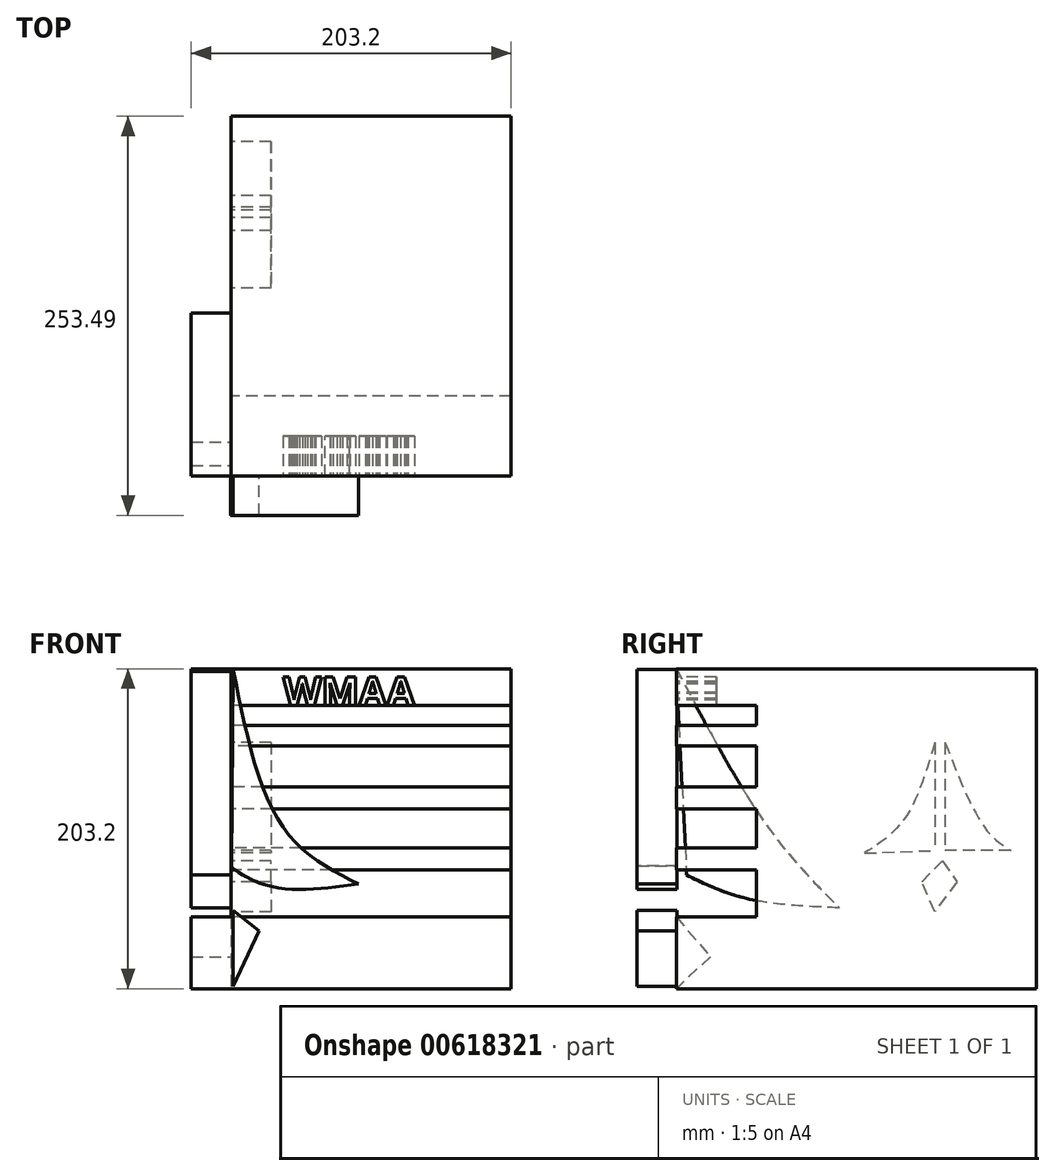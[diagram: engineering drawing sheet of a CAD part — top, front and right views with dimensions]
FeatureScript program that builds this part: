
annotation { "Feature Type Name" : "Feature", "Feature Type Description" : "" }
export const myFeature = defineFeature(function(context is Context, id is Id, definition is map)
    precondition{}
    {
        {
            var Q0;
            Q0=qCreatedBy(makeId("Front.planeOp"),FACE);
            var sketch = newSketch(context, id + "F0", { "sketchPlane" : qUnion([Q0])});
            skLineSegment(sketch, "E0.bottom", {"start": v(88.9, -101.6) * mm, "end": v(-88.9, -101.6) * mm});
            skLineSegment(sketch, "E0.top", {"start": v(88.9, 101.6) * mm, "end": v(-88.9, 101.6) * mm});
            skLineSegment(sketch, "E0.left", {"start": v(88.9, -101.6) * mm, "end": v(88.9, 101.6) * mm});
            skLineSegment(sketch, "E0.right", {"start": v(-88.9, -101.6) * mm, "end": v(-88.9, 101.6) * mm});
            skPoint(sketch, "E0.middle", {"position": v(0, 0) * mm});
            skSolve(sketch);
        }
        {
            var Q0;
            Q0=makeQuery(id+"F0.imprint","IMPRINT",FACE,{"disambiguationData":[TD([[makeQuery(id+"F0.imprint","IMPRINT",EDGE,{"derivedFrom":sQuery(id+"F0.wireOp",EDGE,"E0.bottom")}),-1.0]])]});
            extrude(context, id + "F1", {"entities" : qUnion([Q0]), "depth" : 177.8 * mm, "offsetDistance" : 25.4 * mm});
        }
        {
            var Q0;
            Q0=makeQuery(id+"F1.opExtrude","CAP_FACE",FACE,{"disambiguationData":[OSD([sQuery(id+"F0.wireOp",EDGE,"E0.bottom"),sQuery(id+"F0.wireOp",EDGE,"E0.top"),sQuery(id+"F0.wireOp",EDGE,"E0.left"),sQuery(id+"F0.wireOp",EDGE,"E0.right")])],"isStart":false});
            var sketch = newSketch(context, id + "F2", { "sketchPlane" : qUnion([Q0])});
            skLineSegment(sketch, "E1.bottom", {"start": v(88.9, 52.54) * mm, "end": v(-88.9, 52.54) * mm});
            skLineSegment(sketch, "E1.top", {"start": v(88.9, 65.48) * mm, "end": v(-88.9, 65.48) * mm});
            skLineSegment(sketch, "E1.left", {"start": v(88.9, 52.54) * mm, "end": v(88.9, 65.48) * mm});
            skLineSegment(sketch, "E1.right", {"start": v(-88.9, 52.54) * mm, "end": v(-88.9, 65.48) * mm});
            skPoint(sketch, "E1.middle", {"position": v(0, 59) * mm});
            skLineSegment(sketch, "E2.bottom", {"start": v(88.9, 12.72) * mm, "end": v(-88.9, 12.72) * mm});
            skLineSegment(sketch, "E2.top", {"start": v(88.9, 26.65) * mm, "end": v(-88.9, 26.65) * mm});
            skLineSegment(sketch, "E2.left", {"start": v(88.9, 12.72) * mm, "end": v(88.9, 26.65) * mm});
            skLineSegment(sketch, "E2.right", {"start": v(-88.9, 12.72) * mm, "end": v(-88.9, 26.65) * mm});
            skPoint(sketch, "E2.middle", {"position": v(0, 19.68) * mm});
            skLineSegment(sketch, "E3.bottom", {"start": v(88.9, -26.1) * mm, "end": v(-88.9, -26.1) * mm});
            skLineSegment(sketch, "E3.top", {"start": v(88.9, -12.17) * mm, "end": v(-88.9, -12.17) * mm});
            skLineSegment(sketch, "E3.left", {"start": v(88.9, -26.1) * mm, "end": v(88.9, -12.17) * mm});
            skLineSegment(sketch, "E3.right", {"start": v(-88.9, -26.1) * mm, "end": v(-88.9, -12.17) * mm});
            skPoint(sketch, "E3.middle", {"position": v(0, -19.14) * mm});
            skLineSegment(sketch, "E4.bottom", {"start": v(88.9, -101.6) * mm, "end": v(-88.9, -101.6) * mm});
            skLineSegment(sketch, "E4.top", {"start": v(88.9, -56.14) * mm, "end": v(-88.9, -56.14) * mm});
            skLineSegment(sketch, "E4.left", {"start": v(88.9, -101.6) * mm, "end": v(88.9, -56.14) * mm});
            skLineSegment(sketch, "E4.right", {"start": v(-88.9, -101.6) * mm, "end": v(-88.9, -56.14) * mm});
            skPoint(sketch, "E4.middle", {"position": v(0, -78.87) * mm});
            skSolve(sketch);
        }
        {
            var Q0;
            Q0 = qSketchRegion(id + "F2", true);
            extrude(context, id + "F3", {"entities" : qUnion([Q0]), "operationType" : NewBodyOperationType.ADD, "depth" : 50.8 * mm, "offsetDistance" : 25.4 * mm});
        }
        {
            var Q0;
            {var subQ0=sQuery(id+"F0.wireOp",EDGE,"E0.top");var subQ1=sQuery(id+"F0.wireOp",EDGE,"E0.right");var subQ2=sQuery(id+"F0.wireOp",EDGE,"E0.left");Q0=makeQuery(id+"F3.boolean.opBoolean","SPLIT",FACE,{"disambiguationData":[TD([makeQuery(id+"F1.opExtrude","SWEPT_FACE",FACE,{"disambiguationData":[OSD([subQ0])]})])],"derivedFrom":makeQuery(id+"F1.opExtrude","CAP_FACE",FACE,{"disambiguationData":[OSD([sQuery(id+"F0.wireOp",EDGE,"E0.bottom"),subQ0,subQ2,subQ1])],"isStart":false})});}
            var sketch = newSketch(context, id + "F4", { "sketchPlane" : qUnion([Q0])});
            skLineSegment(sketch, "E5.bottom", {"start": v(88.9, 101.6) * mm, "end": v(-88.9, 101.6) * mm});
            skLineSegment(sketch, "E5.top", {"start": v(88.9, 78.42) * mm, "end": v(-88.9, 78.42) * mm});
            skLineSegment(sketch, "E5.left", {"start": v(88.9, 101.6) * mm, "end": v(88.9, 78.42) * mm});
            skLineSegment(sketch, "E5.right", {"start": v(-88.9, 101.6) * mm, "end": v(-88.9, 78.42) * mm});
            skSolve(sketch);
        }
        {
            var Q0;
            Q0 = qSketchRegion(id + "F4", true);
            extrude(context, id + "F5", {"entities" : qUnion([Q0]), "operationType" : NewBodyOperationType.ADD, "depth" : 50.8 * mm, "offsetDistance" : 25.4 * mm});
        }
        {
            var Q0;
            Q0=qCreatedBy(makeId("Front.planeOp"),FACE);
            cPlane(context, id + "F6", {"entities" : qUnion([Q0]), "cplaneType" : CPlaneType.OFFSET, "offset" : 228.1 * mm, "width" : 152.4 * mm, "height" : 152.4 * mm});
        }
        {
            var Q0;
            Q0=qCreatedBy(id+"F6.planeOp",FACE);
            var sketch = newSketch(context, id + "F7", { "sketchPlane" : qUnion([Q0])});
            skFitSpline(sketch, "E6", {"points": [v(-87.66, 101.32) * mm, v(-55.3, 0) * mm, v(-8.02, -35.07) * mm], "startDerivative": vector(40.82, -203.79) * mm, "endDerivative": vector(122.45, -62.05) * mm});
            skFitSpline(sketch, "E7", {"points": [v(-8.02, -35.07) * mm, v(-69.25, -35.07) * mm, v(-89.16, -23.62) * mm, v(-88.66, -23.62) * mm], "startDerivative": vector(-111.23, -15.45) * mm, "endDerivative": vector(13.28, -2.65) * mm});
            skLineSegment(sketch, "E8", {"start": v(-87.66, 101.32) * mm, "end": v(-88.66, -23.62) * mm});
            skLineSegment(sketch, "E9", {"start": v(-87.66, -52) * mm, "end": v(-71.24, -64.93) * mm});
            skLineSegment(sketch, "E10", {"start": v(-71.24, -64.93) * mm, "end": v(-87.66, -100.28) * mm});
            skLineSegment(sketch, "E11", {"start": v(-87.66, -100.28) * mm, "end": v(-87.66, -52) * mm});
            skSolve(sketch);
        }
        {
            var Q0;
            Q0 = qSketchRegion(id + "F7", true);
            extrude(context, id + "F8", {"entities" : qUnion([Q0]), "operationType" : NewBodyOperationType.ADD, "depth" : 25.4 * mm, "offsetDistance" : 25.4 * mm});
        }
        {
            var Q0;
            Q0=makeQuery(id+"F5.boolean.opBoolean","MERGE",FACE,{"derivedFrom":[makeQuery(id+"F3.boolean.opBoolean","MERGE",FACE,{"derivedFrom":[makeQuery(id+"F1.opExtrude","SWEPT_FACE",FACE,{"disambiguationData":[OSD([sQuery(id+"F0.wireOp",EDGE,"E0.right")])]}),makeQuery(id+"F3.opExtrude","SWEPT_FACE",FACE,{"disambiguationData":[OSD([sQuery(id+"F2.wireOp",EDGE,"E1.right")])]}),makeQuery(id+"F3.opExtrude","SWEPT_FACE",FACE,{"disambiguationData":[OSD([sQuery(id+"F2.wireOp",EDGE,"E2.right")])]}),makeQuery(id+"F3.opExtrude","SWEPT_FACE",FACE,{"disambiguationData":[OSD([sQuery(id+"F2.wireOp",EDGE,"E3.right")])]}),makeQuery(id+"F3.opExtrude","SWEPT_FACE",FACE,{"disambiguationData":[OSD([sQuery(id+"F2.wireOp",EDGE,"E4.right")])]})]}),makeQuery(id+"F5.opExtrude","SWEPT_FACE",FACE,{"disambiguationData":[OSD([sQuery(id+"F4.wireOp",EDGE,"E5.right")])]})]});
            var sketch = newSketch(context, id + "F9", { "sketchPlane" : qUnion([Q0])});
            skFitSpline(sketch, "E12", {"points": [v(228.6, 101.6) * mm, v(169.67, 0) * mm, v(125.03, -50.26) * mm], "startDerivative": vector(-103.47, -196.05) * mm, "endDerivative": vector(-103.69, -103.4) * mm});
            skFitSpline(sketch, "E13", {"points": [v(125.03, -50.26) * mm, v(185.43, -43.96) * mm, v(228.6, -26.1) * mm], "startDerivative": vector(118.97, 4.8) * mm, "endDerivative": vector(87.5, 44.36) * mm});
            skLineSegment(sketch, "E14", {"start": v(228.6, 101.6) * mm, "end": v(228.6, -23.58) * mm});
            skLineSegment(sketch, "E15", {"start": v(228.6, -56.14) * mm, "end": v(206.96, -81.25) * mm});
            skLineSegment(sketch, "E16", {"start": v(206.96, -81.25) * mm, "end": v(228.6, -101.6) * mm});
            skLineSegment(sketch, "E17", {"start": v(228.6, -101.6) * mm, "end": v(228.6, -56.14) * mm});
            skLineSegment(sketch, "E18", {"start": v(228.6, -56.14) * mm, "end": v(228.6, -101.6) * mm});
            skLineSegment(sketch, "E19", {"start": v(228.6, 101.6) * mm, "end": v(228.1, -23.58) * mm});
            skLineSegment(sketch, "E20", {"start": v(228.1, -23.58) * mm, "end": v(228.6, 101.6) * mm});
            skLineSegment(sketch, "E21", {"start": v(228.6, 100.03) * mm, "end": v(222.01, -29.43) * mm});
            skSolve(sketch);
        }
        {
            var Q0;
            Q0 = qSketchRegion(id + "F9", true);
            extrude(context, id + "F10", {"entities" : qUnion([Q0]), "operationType" : NewBodyOperationType.ADD, "depth" : 25.4 * mm, "offsetDistance" : 25.4 * mm});
        }
        {
            var Q0;
            {var subQ0=sQuery(id+"F2.wireOp",EDGE,"E4.bottom");var subQ1=sQuery(id+"F2.wireOp",EDGE,"E4.right");var subQ2=sQuery(id+"F2.wireOp",EDGE,"E4.top");var subQ3=sQuery(id+"F0.wireOp",EDGE,"E0.right");var subQ4=sQuery(id+"F0.wireOp",EDGE,"E0.left");var subQ5=sQuery(id+"F0.wireOp",EDGE,"E0.top");var subQ6=sQuery(id+"F0.wireOp",EDGE,"E0.bottom");var subQ7=sQuery(id+"F9.wireOp",EDGE,"E14");var subQ8=sQuery(id+"F9.wireOp",EDGE,"E13");var subQ9=sQuery(id+"F9.wireOp",EDGE,"E12");var subQ10=sQuery(id+"F4.wireOp",EDGE,"E5.bottom");var subQ11=sQuery(id+"F4.wireOp",EDGE,"E5.right");var subQ12=sQuery(id+"F4.wireOp",EDGE,"E5.top");Q0=makeQuery(id+"F10.boolean.opBoolean","SPLIT",FACE,{"disambiguationData":[TD([makeQuery(id+"F1.opExtrude","SWEPT_FACE",FACE,{"disambiguationData":[OSD([subQ6])]}),makeQuery(id+"F1.opExtrude","CAP_FACE",FACE,{"disambiguationData":[OSD([subQ6,subQ5,subQ4,subQ3])],"isStart":true}),makeQuery(id+"F1.opExtrude","CAP_FACE",FACE,{"disambiguationData":[OSD([subQ6,subQ5,subQ4,subQ3])],"isStart":false}),makeQuery(id+"F1.opExtrude","SWEPT_FACE",FACE,{"disambiguationData":[OSD([subQ5])]}),makeQuery(id+"F3.opExtrude","SWEPT_FACE",FACE,{"disambiguationData":[OSD([sQuery(id+"F2.wireOp",EDGE,"E1.bottom")])]}),makeQuery(id+"F3.opExtrude","SWEPT_FACE",FACE,{"disambiguationData":[OSD([sQuery(id+"F2.wireOp",EDGE,"E1.top")])]}),makeQuery(id+"F3.opExtrude","SWEPT_FACE",FACE,{"disambiguationData":[OSD([sQuery(id+"F2.wireOp",EDGE,"E2.bottom")])]}),makeQuery(id+"F3.opExtrude","SWEPT_FACE",FACE,{"disambiguationData":[OSD([sQuery(id+"F2.wireOp",EDGE,"E2.top")])]}),makeQuery(id+"F3.opExtrude","SWEPT_FACE",FACE,{"disambiguationData":[OSD([subQ0])]}),makeQuery(id+"F3.opExtrude","CAP_FACE",FACE,{"disambiguationData":[OSD([subQ0,subQ2,sQuery(id+"F2.wireOp",EDGE,"E4.left"),subQ1])],"isStart":false}),makeQuery(id+"F3.opExtrude","SWEPT_FACE",FACE,{"disambiguationData":[OSD([subQ2])]}),makeQuery(id+"F5.opExtrude","SWEPT_FACE",FACE,{"disambiguationData":[OSD([subQ10])]}),makeQuery(id+"F5.opExtrude","CAP_FACE",FACE,{"disambiguationData":[OSD([subQ10,subQ12,sQuery(id+"F4.wireOp",EDGE,"E5.left"),subQ11])],"isStart":false}),makeQuery(id+"F5.opExtrude","SWEPT_FACE",FACE,{"disambiguationData":[OSD([subQ12])]}),makeQuery(id+"F10.opExtrude","SWEPT_FACE",FACE,{"disambiguationData":[OSD([subQ9])]}),makeQuery(id+"F10.opExtrude","CAP_FACE",FACE,{"disambiguationData":[OSD([subQ9,subQ8,subQ7,sQuery(id+"F9.wireOp",EDGE,"E21")])],"isStart":true}),makeQuery(id+"F10.opExtrude","SWEPT_FACE",FACE,{"disambiguationData":[OSD([subQ8])]}),makeQuery(id+"F10.opExtrude","SWEPT_FACE",FACE,{"disambiguationData":[OSD([subQ7])]}),makeQuery(id+"F10.opExtrude","SWEPT_FACE",FACE,{"disambiguationData":[OSD([sQuery(id+"F9.wireOp",EDGE,"E15")])]}),makeQuery(id+"F10.opExtrude","SWEPT_FACE",FACE,{"disambiguationData":[OSD([sQuery(id+"F9.wireOp",EDGE,"E16")])]}),makeQuery(id+"F10.opExtrude","SWEPT_FACE",FACE,{"disambiguationData":[OSD([sQuery(id+"F9.wireOp",EDGE,"E18")])]})])],"derivedFrom":makeQuery(id+"F5.boolean.opBoolean","MERGE",FACE,{"derivedFrom":[makeQuery(id+"F3.boolean.opBoolean","MERGE",FACE,{"derivedFrom":[makeQuery(id+"F1.opExtrude","SWEPT_FACE",FACE,{"disambiguationData":[OSD([subQ3])]}),makeQuery(id+"F3.opExtrude","SWEPT_FACE",FACE,{"disambiguationData":[OSD([sQuery(id+"F2.wireOp",EDGE,"E1.right")])]}),makeQuery(id+"F3.opExtrude","SWEPT_FACE",FACE,{"disambiguationData":[OSD([sQuery(id+"F2.wireOp",EDGE,"E2.right")])]}),makeQuery(id+"F3.opExtrude","SWEPT_FACE",FACE,{"disambiguationData":[OSD([sQuery(id+"F2.wireOp",EDGE,"E3.right")])]}),makeQuery(id+"F3.opExtrude","SWEPT_FACE",FACE,{"disambiguationData":[OSD([subQ1])]})]}),makeQuery(id+"F5.opExtrude","SWEPT_FACE",FACE,{"disambiguationData":[OSD([subQ11])]})]})});}
            var sketch = newSketch(context, id + "F11", { "sketchPlane" : qUnion([Q0])});
            skLineSegment(sketch, "E22", {"start": v(57.84, 54.79) * mm, "end": v(57.84, -13.85) * mm});
            skLineSegment(sketch, "E23", {"start": v(64.46, 54.79) * mm, "end": v(64.46, -13.85) * mm});
            skFitSpline(sketch, "E24", {"points": [v(64.46, 54.79) * mm, v(83.9, 6) * mm, v(109.11, -15.5) * mm], "startDerivative": vector(28.71, -98.41) * mm, "endDerivative": vector(61.87, -39.94) * mm});
            skFitSpline(sketch, "E25", {"points": [v(109.11, -15.5) * mm, v(64.46, -13.85) * mm], "startDerivative": vector(-44.66, 1.65) * mm, "endDerivative": vector(-44.66, 1.65) * mm});
            skFitSpline(sketch, "E26", {"points": [v(57.84, 54.79) * mm, v(32.2, 0) * mm, v(16.08, -13.85) * mm], "startDerivative": vector(-40.05, -102.98) * mm, "endDerivative": vector(-43.8, -27.9) * mm});
            skFitSpline(sketch, "E27", {"points": [v(16.08, -13.85) * mm, v(57.84, -13.85) * mm], "startDerivative": vector(41.76, 0) * mm, "endDerivative": vector(41.76, 0) * mm});
            skLineSegment(sketch, "E28", {"start": v(59.5, -20.47) * mm, "end": v(50.4, -33.7) * mm});
            skLineSegment(sketch, "E29", {"start": v(50.4, -33.7) * mm, "end": v(64.46, -52.72) * mm});
            skLineSegment(sketch, "E30", {"start": v(64.46, -52.72) * mm, "end": v(72.73, -33.7) * mm});
            skLineSegment(sketch, "E31", {"start": v(72.73, -33.7) * mm, "end": v(59.5, -20.47) * mm});
            skSolve(sketch);
        }
        {
            var Q0;
            Q0 = qSketchRegion(id + "F11", true);
            extrude(context, id + "F12", {"entities" : qUnion([Q0]), "operationType" : NewBodyOperationType.REMOVE, "oppositeDirection" : true, "depth" : 25.4 * mm, "offsetDistance" : 25.4 * mm});
        }
        {
            var Q0;
            Q0=makeQuery(id+"F10.boolean.opBoolean","MERGE",FACE,{"derivedFrom":[makeQuery(id+"F5.opExtrude","CAP_FACE",FACE,{"disambiguationData":[OSD([sQuery(id+"F4.wireOp",EDGE,"E5.bottom"),sQuery(id+"F4.wireOp",EDGE,"E5.top"),sQuery(id+"F4.wireOp",EDGE,"E5.left"),sQuery(id+"F4.wireOp",EDGE,"E5.right")])],"isStart":false}),makeQuery(id+"F10.opExtrude","SWEPT_FACE",FACE,{"disambiguationData":[OSD([sQuery(id+"F9.wireOp",EDGE,"E14")])]})]});
            var sketch = newSketch(context, id + "F13", { "sketchPlane" : qUnion([Q0])});
            skText(sketch, "E32", { "text": "WMAA", "fontName": "OpenSans-Bold.ttf"});
            const initialGuessF13  = {"E32": [-0.0559, 0.07842, 1, 0, 0.01813]};
            skSetInitialGuess(sketch, initialGuessF13);
            skSolve(sketch);
        }
        {
            var Q0;
            Q0 = qSketchRegion(id + "F13", true);
            extrude(context, id + "F14", {"entities" : qUnion([Q0]), "operationType" : NewBodyOperationType.REMOVE, "oppositeDirection" : true, "depth" : 25.4 * mm, "offsetDistance" : 25.4 * mm});
        }
    });
